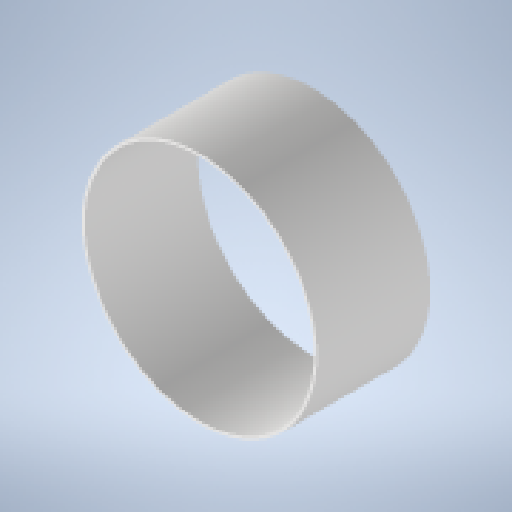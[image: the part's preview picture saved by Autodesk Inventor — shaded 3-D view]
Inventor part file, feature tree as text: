
AUTODESK INVENTOR PART (.ipt)
format: ipt  version: 2023.1 (Build 271208000, 208)  size: 143,360 bytes
history: native  units: mm
features: extrude x1, sketch x1
ambient origin geometry x8: Origin, YZ Plane, XZ Plane, XY Plane, X Axis, Y Axis, Z Axis, Center Point
bodies: Solid1 (feature_tree)
feature tree (2):
  extrude  "Extrusion1"  Depth=80.0mm
  sketch  "Sketch1"  dims[d0=166.0mm d1=2.0mm d2=80.0mm d3=0.0mm]
